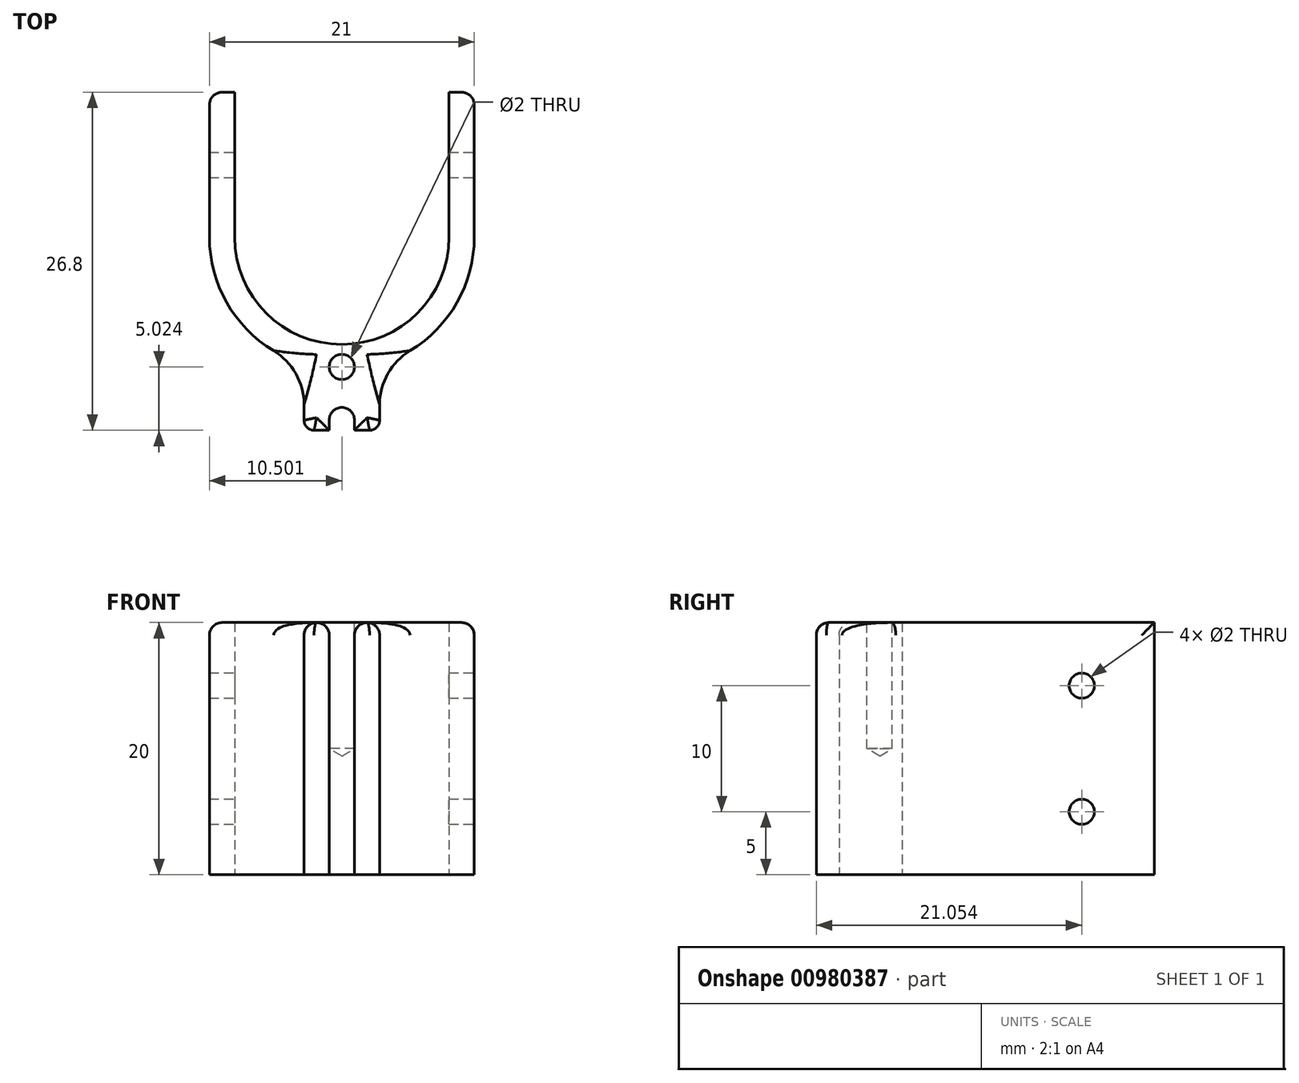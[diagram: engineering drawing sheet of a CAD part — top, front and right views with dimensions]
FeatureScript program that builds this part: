
annotation { "Feature Type Name" : "Feature", "Feature Type Description" : "" }
export const myFeature = defineFeature(function(context is Context, id is Id, definition is map)
    precondition{}
    {
        {
            var Q0;
            Q0=qCreatedBy(makeId("Top.planeOp"),FACE);
            var sketch = newSketch(context, id + "F0", { "sketchPlane" : qUnion([Q0])});
            skArc(sketch, "E0", {"start": v(-31.08, 7.28) * mm, "mid": v(-22.58, -1.22) * mm, "end": v(-14.08, 7.28) * mm});
            skLineSegment(sketch, "E1", {"start": v(-31.08, 7.28) * mm, "end": v(-31.08, 18.78) * mm});
            skLineSegment(sketch, "E2", {"start": v(-14.08, 7.28) * mm, "end": v(-14.08, 18.78) * mm});
            skPoint(sketch, "E3", {"position": v(-22.58, -1.22) * mm});
            skLineSegment(sketch, "E4.0", {"start": v(-33.08, 7.28) * mm, "end": v(-33.08, 18.78) * mm});
            skArc(sketch, "E4.1", {"start": v(-33.08, 7.28) * mm, "mid": v(-31, 1) * mm, "end": v(-25.58, -2.78) * mm});
            skLineSegment(sketch, "E4.2", {"start": v(-12.08, 7.28) * mm, "end": v(-12.08, 18.78) * mm});
            skLineSegment(sketch, "E5", {"start": v(-33.08, 18.78) * mm, "end": v(-31.08, 18.78) * mm});
            skLineSegment(sketch, "E6", {"start": v(-14.08, 18.78) * mm, "end": v(-12.08, 18.78) * mm});
            skLineSegment(sketch, "E7", {"start": v(-22.58, 7.28) * mm, "end": v(-22.58, -1.22) * mm});
            skLineSegment(sketch, "E8", {"start": v(-22.58, -3.22) * mm, "end": v(-22.58, -6.22) * mm});
            skLineSegment(sketch, "E9", {"start": v(-25.58, -2.78) * mm, "end": v(-25.58, -7.22) * mm});
            skLineSegment(sketch, "E10", {"start": v(-19.58, -2.78) * mm, "end": v(-19.58, -7.22) * mm});
            skArc(sketch, "E11.trimOffspring", {"start": v(-19.58, -2.78) * mm, "mid": v(-14.16, 1) * mm, "end": v(-12.08, 7.28) * mm});
            skPoint(sketch, "E12.start.orphan", {"position": v(-21.58, -8.02) * mm});
            skPoint(sketch, "E13.end.orphan", {"position": v(-23.58, -8.02) * mm});
            skArc(sketch, "E14", {"start": v(-21.58, -7.22) * mm, "mid": v(-22.58, -6.22) * mm, "end": v(-23.58, -7.22) * mm});
            skLineSegment(sketch, "E15", {"start": v(-19.58, -7.22) * mm, "end": v(-19.58, -8.02) * mm});
            skLineSegment(sketch, "E16", {"start": v(-19.58, -8.02) * mm, "end": v(-21.58, -8.02) * mm});
            skLineSegment(sketch, "E17", {"start": v(-21.58, -8.02) * mm, "end": v(-21.58, -7.22) * mm});
            skLineSegment(sketch, "E18", {"start": v(-23.58, -7.22) * mm, "end": v(-23.58, -8.02) * mm});
            skLineSegment(sketch, "E19", {"start": v(-23.58, -8.02) * mm, "end": v(-25.58, -8.02) * mm});
            skLineSegment(sketch, "E20", {"start": v(-25.58, -8.02) * mm, "end": v(-25.58, -7.22) * mm});
            skSolve(sketch);
        }
        {
            var Q0;
            Q0 = qSketchRegion(id + "F0", true);
            extrude(context, id + "F1", {"entities" : qUnion([Q0]), "depth" : 20 * mm, "offsetDistance" : 25 * mm});
        }
        {
            var Q0;
            Q0=makeQuery(id+"F1.opExtrude","CAP_FACE",FACE,{"disambiguationData":[OSD([sQuery(id+"F0.wireOp",EDGE,"E0"),sQuery(id+"F0.wireOp",EDGE,"E1"),sQuery(id+"F0.wireOp",EDGE,"E2"),sQuery(id+"F0.wireOp",EDGE,"E4.0"),sQuery(id+"F0.wireOp",EDGE,"E4.1"),sQuery(id+"F0.wireOp",EDGE,"E4.2"),sQuery(id+"F0.wireOp",EDGE,"E5"),sQuery(id+"F0.wireOp",EDGE,"E6"),sQuery(id+"F0.wireOp",EDGE,"E9"),sQuery(id+"F0.wireOp",EDGE,"E10"),sQuery(id+"F0.wireOp",EDGE,"V73vvXux-F9en-iSgE-2xyC-TmJ2Q1jsqhoE"),sQuery(id+"F0.wireOp",EDGE,"WLEuScPg-Rxtc-pKAk-d5hk-CVCbuB6UcoLD"),sQuery(id+"F0.wireOp",EDGE,"E11.trimOffspring")])],"isStart":false});
            var sketch = newSketch(context, id + "F2", { "sketchPlane" : qUnion([Q0])});
            skPoint(sketch, "E21", {"position": v(-22.58, -3) * mm});
            skSolve(sketch);
        }
        {
            var Q0;
            Q0=sQuery(id+"F2.wireOp",VERTEX,"E21");
            var Q1;
            Q1=makeQuery(id+"F1.opExtrude","SWEPT_BODY",BODY,{"disambiguationData":[OSD([sQuery(id+"F0.wireOp",EDGE,"E0"),sQuery(id+"F0.wireOp",EDGE,"E1"),sQuery(id+"F0.wireOp",EDGE,"E2"),sQuery(id+"F0.wireOp",EDGE,"E4.0"),sQuery(id+"F0.wireOp",EDGE,"E4.1"),sQuery(id+"F0.wireOp",EDGE,"E4.2"),sQuery(id+"F0.wireOp",EDGE,"E5"),sQuery(id+"F0.wireOp",EDGE,"E6"),sQuery(id+"F0.wireOp",EDGE,"E9"),sQuery(id+"F0.wireOp",EDGE,"E10"),sQuery(id+"F0.wireOp",EDGE,"V73vvXux-F9en-iSgE-2xyC-TmJ2Q1jsqhoE"),sQuery(id+"F0.wireOp",EDGE,"WLEuScPg-Rxtc-pKAk-d5hk-CVCbuB6UcoLD"),sQuery(id+"F0.wireOp",EDGE,"E11.trimOffspring")])]});
            hole(context, id + "F3", {"style" : HoleStyle.SIMPLE, "endStyle" : HoleEndStyle.BLIND, "holeDiameter" : 2 * mm, "majorDiameter" : 5 * mm, "holeDepth" : 10 * mm, "isTappedThrough" : true, "tappedDepth" : 12 * mm, "tapClearance" : 3, "locations" : qUnion([Q0]), "scope" : qUnion([Q1])});
        }
        {
            var Q0;
            Q0=makeQuery(id+"F1.opExtrude","SWEPT_FACE",FACE,{"disambiguationData":[OSD([sQuery(id+"F0.wireOp",EDGE,"E4.2")])]});
            var sketch = newSketch(context, id + "F4", { "sketchPlane" : qUnion([Q0])});
            skPoint(sketch, "E22", {"position": v(13.03, 15) * mm});
            skPoint(sketch, "E22.positionSnap0", {"position": v(13.03, 20) * mm});
            skPoint(sketch, "E23", {"position": v(13.03, 5) * mm});
            skPoint(sketch, "E23.positionSnap0", {"position": v(13.03, 0) * mm});
            skSolve(sketch);
        }
        {
            var Q0;
            Q0=sQuery(id+"F4.wireOp",VERTEX,"E22");
            var Q1;
            Q1=sQuery(id+"F4.wireOp",VERTEX,"E23");
            var Q2;
            Q2=makeQuery(id+"F1.opExtrude","SWEPT_BODY",BODY,{"disambiguationData":[OSD([sQuery(id+"F0.wireOp",EDGE,"E0"),sQuery(id+"F0.wireOp",EDGE,"E1"),sQuery(id+"F0.wireOp",EDGE,"E2"),sQuery(id+"F0.wireOp",EDGE,"E4.0"),sQuery(id+"F0.wireOp",EDGE,"E4.1"),sQuery(id+"F0.wireOp",EDGE,"E4.2"),sQuery(id+"F0.wireOp",EDGE,"E5"),sQuery(id+"F0.wireOp",EDGE,"E6"),sQuery(id+"F0.wireOp",EDGE,"E9"),sQuery(id+"F0.wireOp",EDGE,"E10"),sQuery(id+"F0.wireOp",EDGE,"V73vvXux-F9en-iSgE-2xyC-TmJ2Q1jsqhoE"),sQuery(id+"F0.wireOp",EDGE,"WLEuScPg-Rxtc-pKAk-d5hk-CVCbuB6UcoLD"),sQuery(id+"F0.wireOp",EDGE,"E11.trimOffspring")])]});
            hole(context, id + "F5", {"style" : HoleStyle.SIMPLE, "endStyle" : HoleEndStyle.THROUGH, "holeDiameter" : 2 * mm, "majorDiameter" : 5 * mm, "isTappedThrough" : true, "tappedDepth" : 12 * mm, "tapClearance" : 3, "locations" : qUnion([Q0, Q1]), "scope" : qUnion([Q2])});
        }
        {
            var Q0;
            Q0=makeQuery(id+"F1.opExtrude","CAP_EDGE",EDGE,{"disambiguationData":[OSD([sQuery(id+"F0.wireOp",EDGE,"E4.2")])],"isStart":false});
            var Q1;
            Q1=makeQuery(id+"F1.opExtrude","CAP_EDGE",EDGE,{"disambiguationData":[OSD([sQuery(id+"F0.wireOp",EDGE,"E4.1")])],"isStart":false});
            var Q2;
            Q2=makeQuery(id+"F1.opExtrude","CAP_EDGE",EDGE,{"disambiguationData":[OSD([sQuery(id+"F0.wireOp",EDGE,"E9")])],"isStart":false});
            var Q3;
            Q3=makeQuery(id+"F1.opExtrude","CAP_EDGE",EDGE,{"disambiguationData":[OSD([sQuery(id+"F0.wireOp",EDGE,"E10")])],"isStart":false});
            var Q4;
            Q4=makeQuery(id+"F1.opExtrude","CAP_EDGE",EDGE,{"disambiguationData":[OSD([sQuery(id+"F0.wireOp",EDGE,"BCqoNenQ-0Y1a-VVUj-MyCL-OegwBNkN3W4E")])],"isStart":false});
            var Q5;
            Q5=makeQuery(id+"F1.opExtrude","CAP_EDGE",EDGE,{"disambiguationData":[OSD([sQuery(id+"F0.wireOp",EDGE,"U8P9LnE8-RtIZ-4FFE-mMJ2-ffdSx626deKX")])],"isStart":false});
            var Q6;
            Q6=makeQuery(id+"F1.opExtrude","SWEPT_EDGE",EDGE,{"disambiguationData":[OSD([sQuery(id+"F0.wireOp",EDGE,"E4.0"),sQuery(id+"F0.wireOp",EDGE,"E5")])]});
            var Q7;
            Q7=makeQuery(id+"F1.opExtrude","SWEPT_EDGE",EDGE,{"disambiguationData":[OSD([sQuery(id+"F0.wireOp",EDGE,"E4.2"),sQuery(id+"F0.wireOp",EDGE,"E6")])]});
            var Q8;
            Q8=makeQuery(id+"F1.opExtrude","CAP_EDGE",EDGE,{"disambiguationData":[OSD([sQuery(id+"F0.wireOp",EDGE,"E14")])],"isStart":false});
            var Q9;
            Q9=makeQuery(id+"F1.opExtrude","CAP_EDGE",EDGE,{"disambiguationData":[OSD([sQuery(id+"F0.wireOp",EDGE,"E17")])],"isStart":false});
            var Q10;
            Q10=makeQuery(id+"F1.opExtrude","CAP_EDGE",EDGE,{"disambiguationData":[OSD([sQuery(id+"F0.wireOp",EDGE,"E18")])],"isStart":false});
            var Q11;
            Q11=makeQuery(id+"F1.opExtrude","CAP_EDGE",EDGE,{"disambiguationData":[OSD([sQuery(id+"F0.wireOp",EDGE,"E16")])],"isStart":false});
            var Q12;
            Q12=makeQuery(id+"F1.opExtrude","CAP_EDGE",EDGE,{"disambiguationData":[OSD([sQuery(id+"F0.wireOp",EDGE,"E19")])],"isStart":false});
            var Q13;
            Q13=makeQuery(id+"F3.hole-0.boolean.opBoolean","COPY",EDGE,{"derivedFrom":makeQuery(id+"F3.hole-0.opRevolve","SWEPT_EDGE",EDGE,{"disambiguationData":[OSD([sQuery(id+"F3.hole-0.sketch.wireOp",EDGE,"core_line_2"),sQuery(id+"F3.hole-0.sketch.wireOp",EDGE,"core_line_3")])]})});
            fillet(context, id + "F6", {"entities" : qUnion([Q0, Q1, Q2, Q3, Q4, Q5, Q6, Q7, Q8, Q9, Q10, Q11, Q12, Q13]), "radius" : 1 * mm, "tangentPropagation" : true, "allowEdgeOverflow" : false});
        }
        {
            var Q0;
            Q0=makeQuery(id+"F1.opExtrude","SWEPT_EDGE",EDGE,{"disambiguationData":[OSD([sQuery(id+"F0.wireOp",EDGE,"E10"),sQuery(id+"F0.wireOp",EDGE,"E11.trimOffspring")])]});
            var Q1;
            Q1=makeQuery(id+"F1.opExtrude","SWEPT_EDGE",EDGE,{"disambiguationData":[OSD([sQuery(id+"F0.wireOp",EDGE,"E4.1"),sQuery(id+"F0.wireOp",EDGE,"E9")])]});
            fillet(context, id + "F7", {"entities" : qUnion([Q0, Q1]), "radius" : 5 * mm, "tangentPropagation" : true, "allowEdgeOverflow" : false});
        }
        {
            var Q0;
            Q0=makeQuery(id+"F1.opExtrude","SWEPT_EDGE",EDGE,{"disambiguationData":[OSD([sQuery(id+"F0.wireOp",EDGE,"E9"),sQuery(id+"F0.wireOp",EDGE,"U8P9LnE8-RtIZ-4FFE-mMJ2-ffdSx626deKX")])]});
            var Q1;
            Q1=makeQuery(id+"F1.opExtrude","SWEPT_EDGE",EDGE,{"disambiguationData":[OSD([sQuery(id+"F0.wireOp",EDGE,"GXsCcWjj-LNWD-NC6I-dgRH-e6b34z8ZcXfT"),sQuery(id+"F0.wireOp",EDGE,"BCqoNenQ-0Y1a-VVUj-MyCL-OegwBNkN3W4E")])]});
            var Q2;
            Q2=makeQuery(id+"F1.opExtrude","SWEPT_EDGE",EDGE,{"disambiguationData":[OSD([sQuery(id+"F0.wireOp",EDGE,"GXsCcWjj-LNWD-NC6I-dgRH-e6b34z8ZcXfT"),sQuery(id+"F0.wireOp",EDGE,"U8P9LnE8-RtIZ-4FFE-mMJ2-ffdSx626deKX")])]});
            var Q3;
            Q3=makeQuery(id+"F1.opExtrude","SWEPT_EDGE",EDGE,{"disambiguationData":[OSD([sQuery(id+"F0.wireOp",EDGE,"E10"),sQuery(id+"F0.wireOp",EDGE,"BCqoNenQ-0Y1a-VVUj-MyCL-OegwBNkN3W4E")])]});
            var Q4;
            Q4=makeQuery(id+"F1.opExtrude","SWEPT_EDGE",EDGE,{"disambiguationData":[OSD([sQuery(id+"F0.wireOp",EDGE,"E15"),sQuery(id+"F0.wireOp",EDGE,"E16")])]});
            var Q5;
            Q5=makeQuery(id+"F1.opExtrude","SWEPT_EDGE",EDGE,{"disambiguationData":[OSD([sQuery(id+"F0.wireOp",EDGE,"E19"),sQuery(id+"F0.wireOp",EDGE,"E20")])]});
            fillet(context, id + "F8", {"entities" : qUnion([Q0, Q1, Q2, Q3, Q4, Q5]), "radius" : 0.8 * mm, "tangentPropagation" : true, "allowEdgeOverflow" : false});
        }
    });
